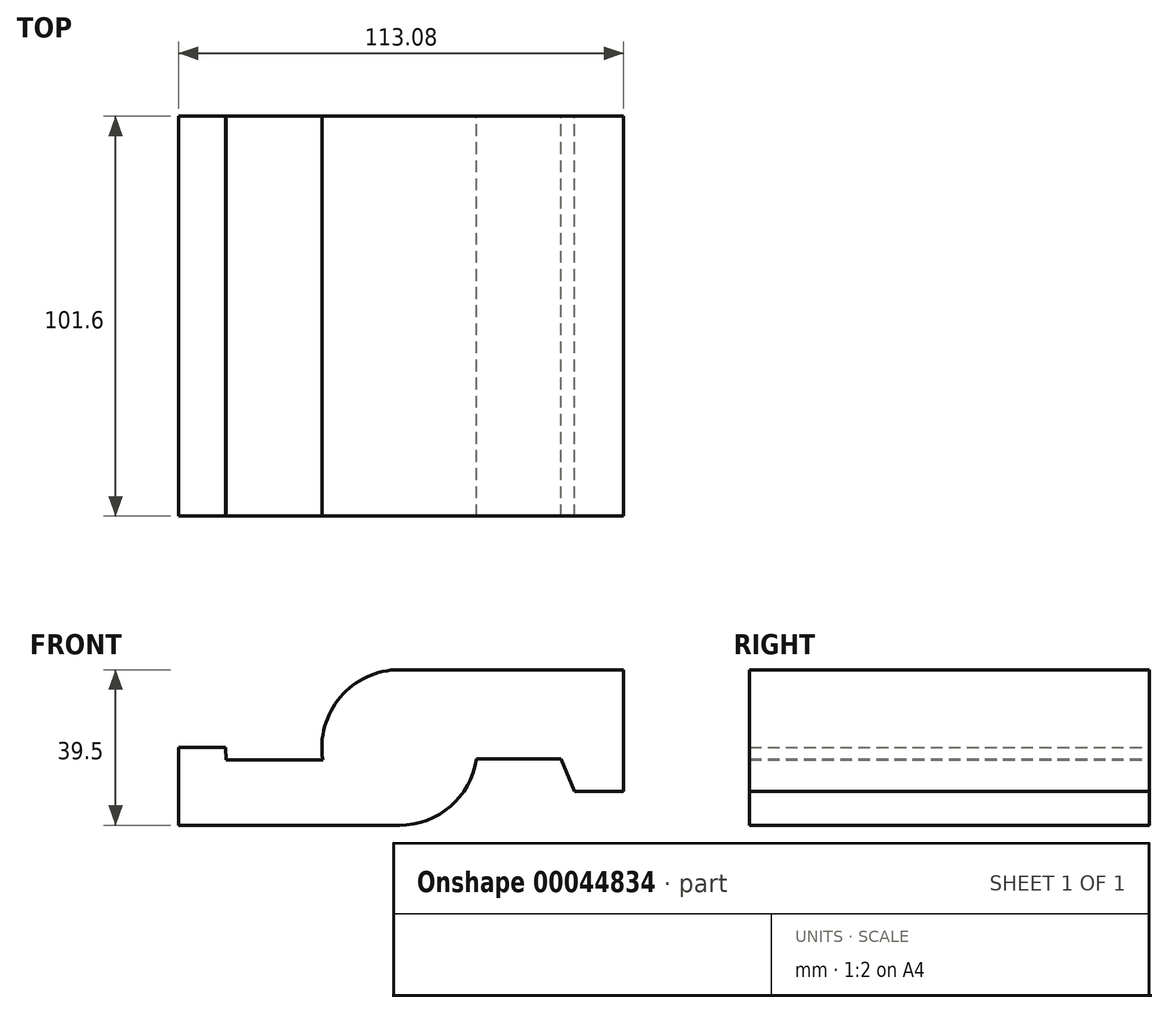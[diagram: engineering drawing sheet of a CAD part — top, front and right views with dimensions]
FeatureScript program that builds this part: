
annotation { "Feature Type Name" : "Feature", "Feature Type Description" : "" }
export const myFeature = defineFeature(function(context is Context, id is Id, definition is map)
    precondition{}
    {
        {
            var Q0;
            Q0=qCreatedBy(makeId("Front.planeOp"),FACE);
            var sketch = newSketch(context, id + "F0", { "sketchPlane" : qUnion([Q0])});
            skCircle(sketch, "E0", {"center": v(0, 0) * mm, "radius": 19.75 * mm});
            skLineSegment(sketch, "E1", {"start": v(0, 19.75) * mm, "end": v(56.94, 19.75) * mm});
            skLineSegment(sketch, "E2", {"start": v(56.94, 19.75) * mm, "end": v(56.94, -11.17) * mm});
            skLineSegment(sketch, "E3", {"start": v(56.94, -11.17) * mm, "end": v(44.44, -11.17) * mm});
            skLineSegment(sketch, "E4", {"start": v(44.44, -11.17) * mm, "end": v(40.98, -2.94) * mm});
            skLineSegment(sketch, "E5", {"start": v(40.98, -2.94) * mm, "end": v(19.53, -2.94) * mm});
            skLineSegment(sketch, "E6", {"start": v(0, -19.75) * mm, "end": v(-56.14, -19.75) * mm});
            skLineSegment(sketch, "E7", {"start": v(-56.14, -19.75) * mm, "end": v(-56.14, 0) * mm});
            skLineSegment(sketch, "E8", {"start": v(-56.14, 0) * mm, "end": v(-44.17, 0) * mm});
            skLineSegment(sketch, "E9", {"start": v(-44.17, 0) * mm, "end": v(-44.06, -3.19) * mm});
            skLineSegment(sketch, "E10", {"start": v(-44.06, -3.19) * mm, "end": v(-19.5, -3.19) * mm});
            skSolve(sketch);
        }
        {
            var Q0;
            {var subQ2=sQuery(id+"F0.wireOp",EDGE,"E6");Q0=makeQuery(id+"F0.imprint","IMPRINT",FACE,{"disambiguationData":[TD([[makeQuery(id+"F0.imprint","IMPRINT",EDGE,{"derivedFrom":subQ2}),-1.0]])]});}
            var Q1;
            {var subQ0=sQuery(id+"F0.wireOp",EDGE,"E0");var subQ2=makeQuery(id+"F0.imprint","INTERSECT",VERTEX,{"derivedFrom":[subQ0,sQuery(id+"F0.wireOp",EDGE,"E1")]});Q1=makeQuery(id+"F0.imprint","IMPRINT",FACE,{"disambiguationData":[TD([[makeQuery(id+"F0.imprint","IMPRINT",EDGE,{"disambiguationData":[TD([[subQ2,-1.0]])],"derivedFrom":subQ0}),1.0]])]});}
            var Q2;
            {var subQ2=sQuery(id+"F0.wireOp",EDGE,"E1");Q2=makeQuery(id+"F0.imprint","IMPRINT",FACE,{"disambiguationData":[TD([[makeQuery(id+"F0.imprint","IMPRINT",EDGE,{"derivedFrom":subQ2}),-1.0]])]});}
            extrude(context, id + "F1", {"entities" : qUnion([Q0, Q1, Q2]), "depth" : 101.6 * mm});
        }
    });
